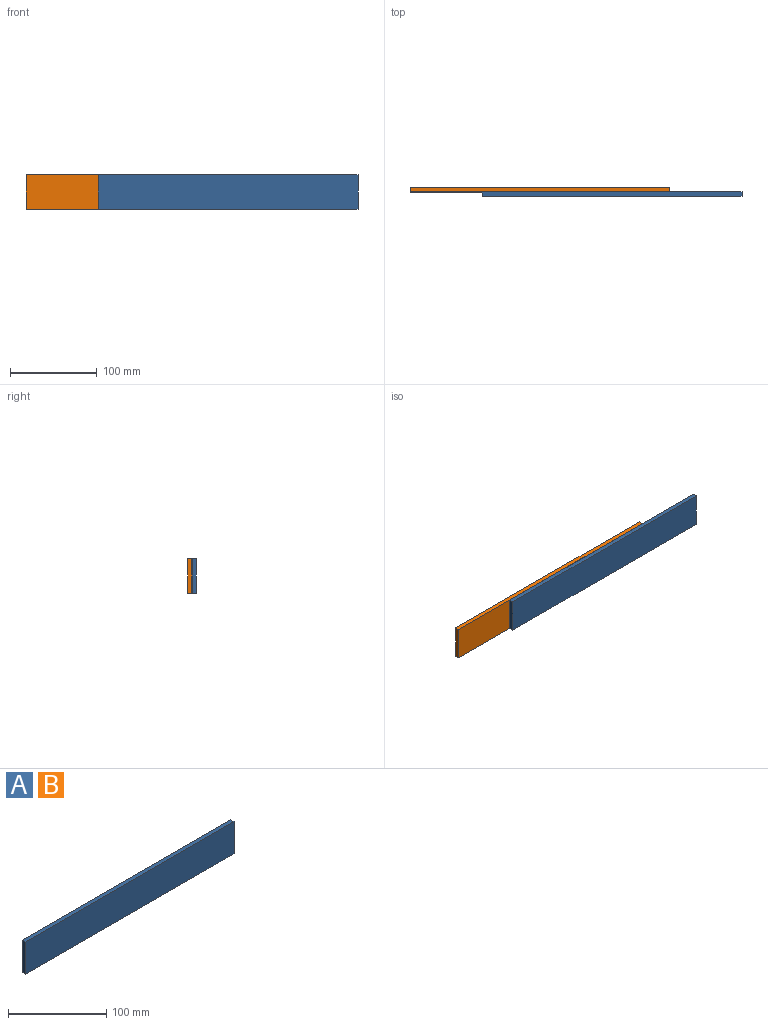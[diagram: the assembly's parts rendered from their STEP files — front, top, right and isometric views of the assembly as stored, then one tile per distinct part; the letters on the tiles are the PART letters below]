
ASSEMBLY  parts=2 mates=1
PART A: 6 faces, bbox 300x5x40 mm
  f0: plane 300x40mm, normal (0,-1,0), area 12000mm2, adj f1,f3,f4,f5
  f1: plane 40x5mm, normal (1,0,0), area 200mm2, adj f0,f2,f4,f5
  f2: plane 300x40mm, normal (0,1,0), area 12000mm2, adj f1,f3,f4,f5
  f3: plane 40x5mm, normal (-1,0,0), area 200mm2, adj f0,f2,f4,f5
  f4: plane 300x5mm, normal (0,0,1), area 1500mm2, adj f0,f1,f2,f3
  f5: plane 300x5mm, normal (0,0,-1), area 1500mm2, adj f0,f1,f2,f3
PART B: same geometry as A
PLACE A t=(82.64,-19.87,5.33)mm
PLACE B t=(-0.85,-14.87,5.33)mm fixed
MATE planar B.f0 <-> A.f2  axis (0,-1,0) through (-0.85,-17.37,25.33)mm
